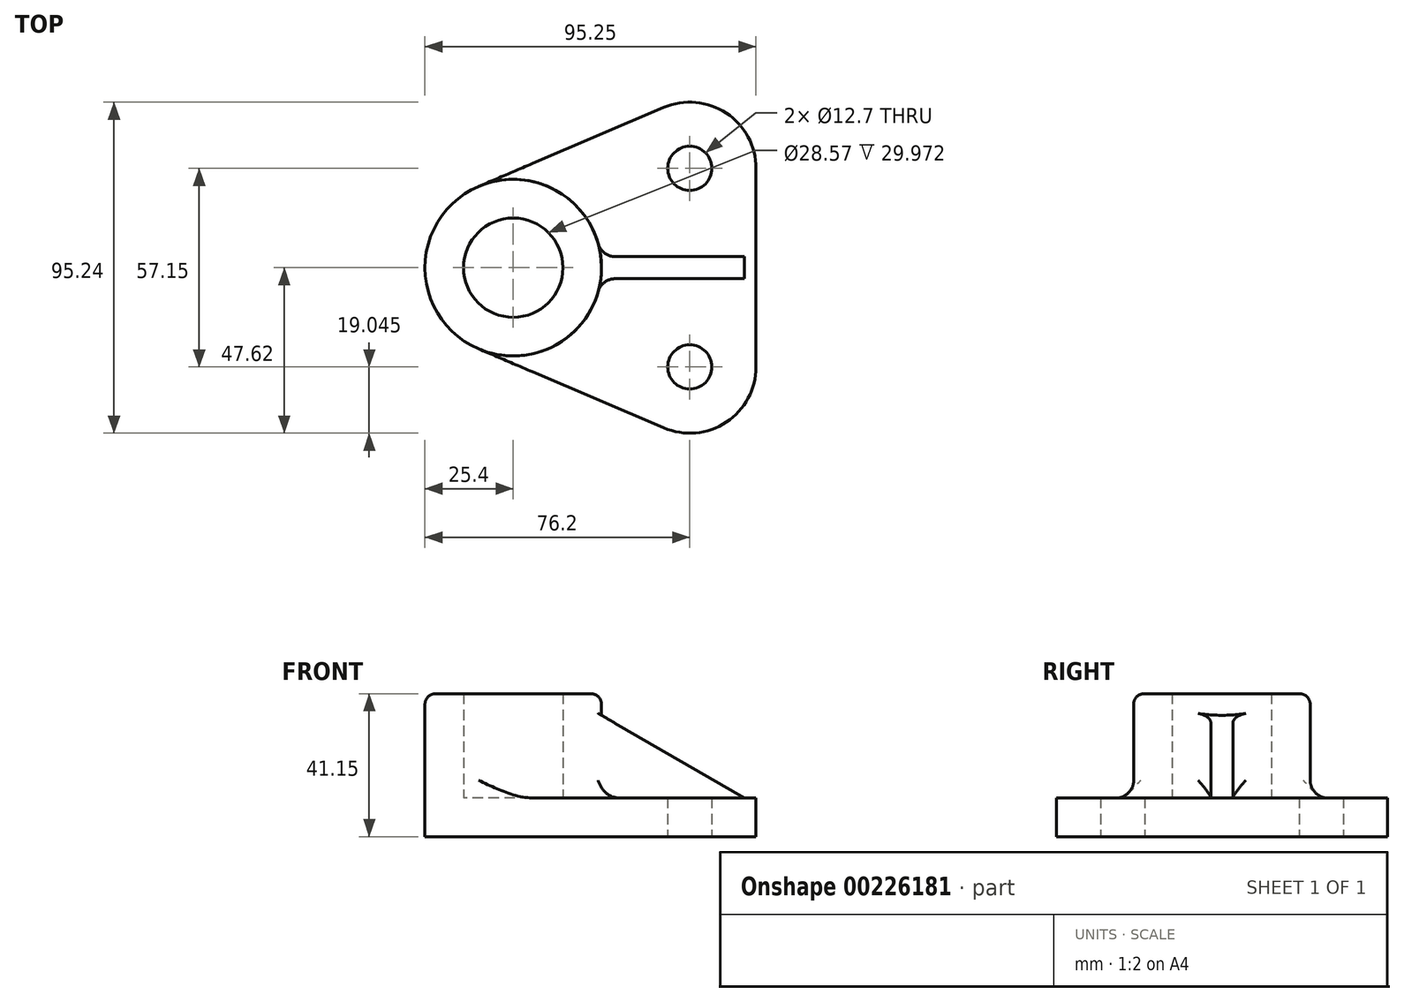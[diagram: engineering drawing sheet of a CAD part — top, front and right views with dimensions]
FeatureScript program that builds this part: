
annotation { "Feature Type Name" : "Feature", "Feature Type Description" : "" }
export const myFeature = defineFeature(function(context is Context, id is Id, definition is map)
    precondition{}
    {
        {
            var Q0;
            Q0=qCreatedBy(makeId("Top.planeOp"),FACE);
            var sketch = newSketch(context, id + "F0", { "sketchPlane" : qUnion([Q0])});
            skCircle(sketch, "E0", {"center": v(0, 0) * mm, "radius": 14.29 * mm});
            skCircle(sketch, "E1", {"center": v(0, 0) * mm, "radius": 25.4 * mm});
            skSolve(sketch);
        }
        {
            var Q0;
            Q0=qCreatedBy(makeId("Top.planeOp"),FACE);
            var sketch = newSketch(context, id + "F1", { "sketchPlane" : qUnion([Q0])});
            skCircle(sketch, "E2", {"center": v(50.8, -28.58) * mm, "radius": 6.35 * mm});
            skCircle(sketch, "E3", {"center": v(50.8, 28.58) * mm, "radius": 6.35 * mm});
            skArc(sketch, "E4", {"start": v(69.85, 28.58) * mm, "mid": v(61.3, 44.47) * mm, "end": v(43.33, 46.1) * mm});
            skArc(sketch, "E5", {"start": v(69.85, -28.58) * mm, "mid": v(61.3, -44.47) * mm, "end": v(43.33, -46.1) * mm});
            skLineSegment(sketch, "E6", {"start": v(69.85, 28.58) * mm, "end": v(69.85, -28.58) * mm});
            skLineSegment(sketch, "E7", {"start": v(43.33, -46.1) * mm, "end": v(-9.97, -23.36) * mm});
            skLineSegment(sketch, "E8", {"start": v(43.33, 46.1) * mm, "end": v(-9.97, 23.36) * mm});
            skLineSegment(sketch, "E9", {"start": v(0, 0) * mm, "end": v(69.85, 0) * mm, "construction": true});
            skCircle(sketch, "E10.0", {"center": v(0, 0) * mm, "radius": 25.4 * mm});
            skSolve(sketch);
        }
        {
            var Q0;
            Q0 = qSketchRegion(id + "F1", true);
            extrude(context, id + "F2", {"entities" : qUnion([Q0]), "depth" : 11.18 * mm});
        }
        {
            var Q0;
            Q0=makeQuery(id+"F0.imprint","IMPRINT",FACE,{"disambiguationData":[TD([[makeQuery(id+"F0.imprint","IMPRINT",EDGE,{"derivedFrom":sQuery(id+"F0.wireOp",EDGE,"E0")}),-1.0]])]});
            extrude(context, id + "F3", {"entities" : qUnion([Q0]), "operationType" : NewBodyOperationType.ADD, "depth" : 41.15 * mm});
        }
        {
            var Q0;
            Q0=makeQuery(id+"F3.opExtrude","CAP_EDGE",EDGE,{"disambiguationData":[OSD([sQuery(id+"F0.wireOp",EDGE,"E1")])],"isStart":false});
            fillet(context, id + "F4", {"entities" : qUnion([Q0]), "radius" : 3.05 * mm, "tangentPropagation" : true, "allowEdgeOverflow" : false});
        }
        {
            var Q0;
            Q0=qCreatedBy(makeId("Front.planeOp"),FACE);
            var sketch = newSketch(context, id + "F5", { "sketchPlane" : qUnion([Q0])});
            skLineSegment(sketch, "E11", {"start": v(19.91, 38.1) * mm, "end": v(19.91, 11.18) * mm});
            skLineSegment(sketch, "E12", {"start": v(19.91, 38.1) * mm, "end": v(66.55, 11.18) * mm});
            skLineSegment(sketch, "E13", {"start": v(66.55, 11.18) * mm, "end": v(19.91, 11.18) * mm});
            skSolve(sketch);
        }
        {
            var Q0;
            Q0 = qSketchRegion(id + "F5", true);
            extrude(context, id + "F6", {"entities" : qUnion([Q0]), "operationType" : NewBodyOperationType.ADD, "endBound" : BoundingType.SYMMETRIC, "depth" : 6.35 * mm});
        }
        {
            var Q0;
            Q0=makeQuery(id+"F6.opExtrude","CAP_EDGE",EDGE,{"disambiguationData":[OSD([sQuery(id+"F5.wireOp",EDGE,"8316de65-d98f-4059-8588-2b977080ebb4.0"),sQuery(id+"F5.wireOp",EDGE,"36afb251-3fe2-49b8-9ab4-004291a34322.0")])],"isStart":false});
            var Q1;
            Q1=makeQuery(id+"F6.boolean.opBoolean","INTERSECT",EDGE,{"derivedFrom":[makeQuery(id+"F3.opExtrude","SWEPT_FACE",FACE,{"disambiguationData":[OSD([sQuery(id+"F0.wireOp",EDGE,"E1")])]}),makeQuery(id+"F6.opExtrude","CAP_FACE",FACE,{"disambiguationData":[OSD([sQuery(id+"F5.wireOp",EDGE,"E11"),sQuery(id+"F5.wireOp",EDGE,"8316de65-d98f-4059-8588-2b977080ebb4.0"),sQuery(id+"F5.wireOp",EDGE,"36afb251-3fe2-49b8-9ab4-004291a34322.0"),sQuery(id+"F5.wireOp",EDGE,"E12")])],"isStart":false})]});
            var Q2;
            Q2=makeQuery(id+"F6.boolean.opBoolean","INTERSECT",EDGE,{"derivedFrom":[makeQuery(id+"F3.opExtrude","SWEPT_FACE",FACE,{"disambiguationData":[OSD([sQuery(id+"F0.wireOp",EDGE,"E1")])]}),makeQuery(id+"F6.opExtrude","CAP_FACE",FACE,{"disambiguationData":[OSD([sQuery(id+"F5.wireOp",EDGE,"E11"),sQuery(id+"F5.wireOp",EDGE,"8316de65-d98f-4059-8588-2b977080ebb4.0"),sQuery(id+"F5.wireOp",EDGE,"36afb251-3fe2-49b8-9ab4-004291a34322.0"),sQuery(id+"F5.wireOp",EDGE,"E12")])],"isStart":true})]});
            var Q3;
            Q3=makeQuery(id+"F6.opExtrude","CAP_EDGE",EDGE,{"disambiguationData":[OSD([sQuery(id+"F5.wireOp",EDGE,"8316de65-d98f-4059-8588-2b977080ebb4.0"),sQuery(id+"F5.wireOp",EDGE,"36afb251-3fe2-49b8-9ab4-004291a34322.0")])],"isStart":true});
            var Q4;
            Q4=makeQuery(id+"F6.opExtrude","CAP_EDGE",EDGE,{"disambiguationData":[OSD([sQuery(id+"F5.wireOp",EDGE,"E13")])],"isStart":false});
            var Q5;
            Q5=makeQuery(id+"F6.opExtrude","CAP_EDGE",EDGE,{"disambiguationData":[OSD([sQuery(id+"F5.wireOp",EDGE,"E13")])],"isStart":true});
            var Q6;
            {var subQ0=makeQuery(id+"F3.opExtrude","SWEPT_FACE",FACE,{"disambiguationData":[OSD([sQuery(id+"F0.wireOp",EDGE,"E1")])]});var subQ1=sQuery(id+"F1.wireOp",EDGE,"E10.0");var subQ2=sQuery(id+"F1.wireOp",EDGE,"E7");var subQ3=makeQuery(id+"F2.opExtrude","CAP_FACE",FACE,{"disambiguationData":[OSD([sQuery(id+"F1.wireOp",EDGE,"E2"),sQuery(id+"F1.wireOp",EDGE,"E3"),sQuery(id+"F1.wireOp",EDGE,"E4"),sQuery(id+"F1.wireOp",EDGE,"E5"),sQuery(id+"F1.wireOp",EDGE,"E6"),subQ2,sQuery(id+"F1.wireOp",EDGE,"E8"),subQ1])],"isStart":false});Q6=makeQuery(id+"F6.boolean.opBoolean","SPLIT",EDGE,{"disambiguationData":[TD([makeQuery(id+"F2.opExtrude","SWEPT_FACE",FACE,{"disambiguationData":[OSD([subQ2])]})])],"derivedFrom":makeQuery(id+"F3.boolean.opBoolean","INTERSECT",EDGE,{"derivedFrom":[subQ3,subQ0]})});}
            var Q7;
            {var subQ0=makeQuery(id+"F3.opExtrude","SWEPT_FACE",FACE,{"disambiguationData":[OSD([sQuery(id+"F0.wireOp",EDGE,"E1")])]});var subQ1=sQuery(id+"F1.wireOp",EDGE,"E10.0");var subQ2=sQuery(id+"F1.wireOp",EDGE,"E8");var subQ3=makeQuery(id+"F2.opExtrude","CAP_FACE",FACE,{"disambiguationData":[OSD([sQuery(id+"F1.wireOp",EDGE,"E2"),sQuery(id+"F1.wireOp",EDGE,"E3"),sQuery(id+"F1.wireOp",EDGE,"E4"),sQuery(id+"F1.wireOp",EDGE,"E5"),sQuery(id+"F1.wireOp",EDGE,"E6"),sQuery(id+"F1.wireOp",EDGE,"E7"),subQ2,subQ1])],"isStart":false});Q7=makeQuery(id+"F6.boolean.opBoolean","SPLIT",EDGE,{"disambiguationData":[TD([makeQuery(id+"F2.opExtrude","SWEPT_FACE",FACE,{"disambiguationData":[OSD([subQ2])]})])],"derivedFrom":makeQuery(id+"F3.boolean.opBoolean","INTERSECT",EDGE,{"derivedFrom":[subQ3,subQ0]})});}
            fillet(context, id + "F7", {"entities" : qUnion([Q0, Q1, Q2, Q3, Q4, Q5, Q6, Q7]), "radius" : 5.08 * mm, "tangentPropagation" : true, "allowEdgeOverflow" : false});
        }
    });
